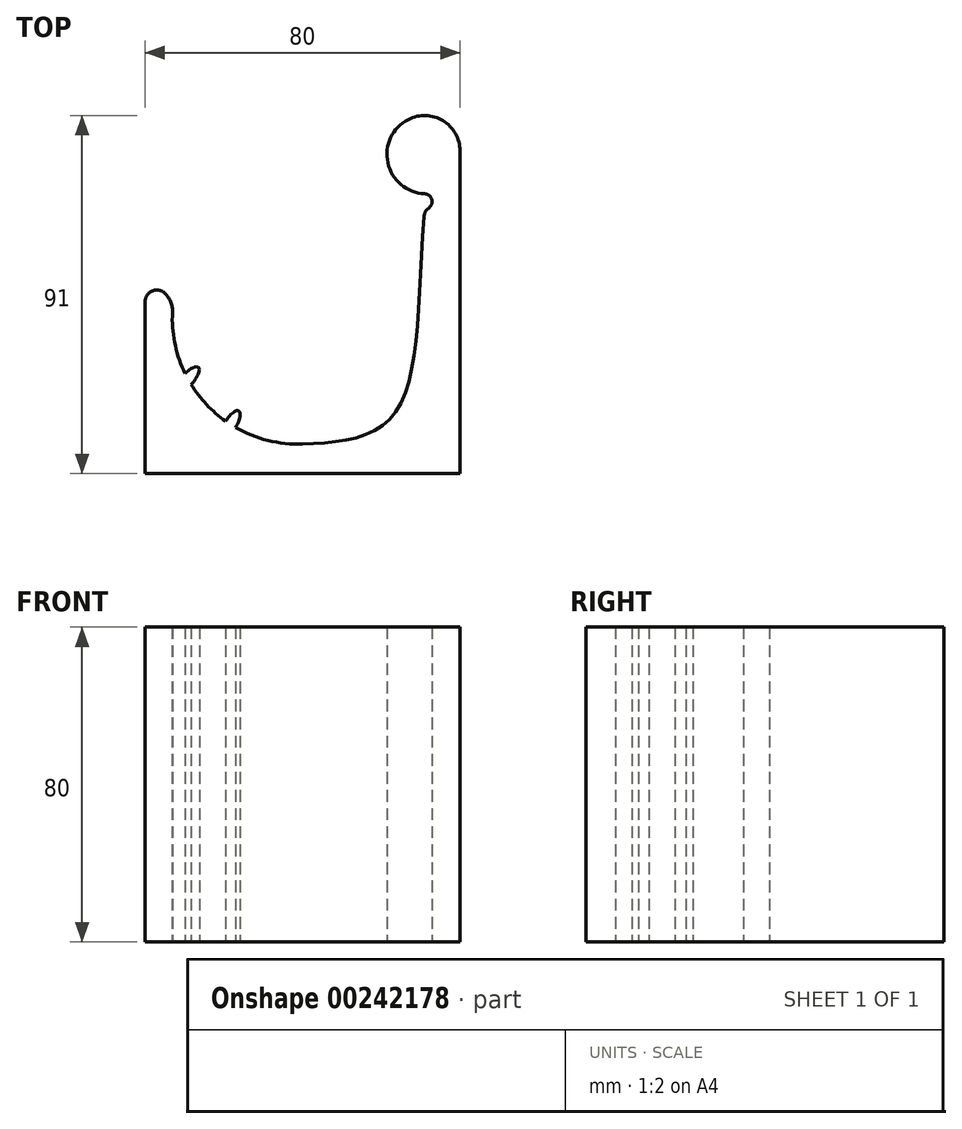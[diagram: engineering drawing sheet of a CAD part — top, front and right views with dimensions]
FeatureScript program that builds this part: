
annotation { "Feature Type Name" : "Feature", "Feature Type Description" : "" }
export const myFeature = defineFeature(function(context is Context, id is Id, definition is map)
    precondition{}
    {
        {
            var Q0;
            Q0=qCreatedBy(makeId("Top.planeOp"),FACE);
            var sketch = newSketch(context, id + "F0", { "sketchPlane" : qUnion([Q0])});
            skLineSegment(sketch, "E0.top", {"start": v(-40, -41) * mm, "end": v(40, -41) * mm});
            skLineSegment(sketch, "E0.left", {"start": v(-40, 7) * mm, "end": v(-40, -41) * mm});
            skLineSegment(sketch, "E0.right", {"start": v(40, 41) * mm, "end": v(40, -41) * mm});
            skPoint(sketch, "E0.middle", {"position": v(0, 0) * mm});
            skArc(sketch, "E1", {"start": v(40, 41) * mm, "mid": v(35.68, 48.68) * mm, "end": v(26.88, 49) * mm});
            skArc(sketch, "E2", {"start": v(26.88, 49) * mm, "mid": v(21.69, 37.98) * mm, "end": v(31, 30.12) * mm});
            skArc(sketch, "E3", {"start": v(31, 30.12) * mm, "mid": v(32.9, 28.12) * mm, "end": v(31, 26.13) * mm});
            skFitSpline(sketch, "E4", {"points": [v(31, 26.13) * mm, v(22.67, -26.58) * mm, v(0, -33.48) * mm], "startDerivative": vector(-9.3, -119.56) * mm, "endDerivative": vector(-66.14, -2.22) * mm});
            skArc(sketch, "E5", {"start": v(0, -33.48) * mm, "mid": v(-8.78, -32.56) * mm, "end": v(-16.97, -29.28) * mm});
            skPoint(sketch, "E6.orphan", {"position": v(-40, 41) * mm});
            skPoint(sketch, "E7.center.orphan", {"position": v(-42.03, 0) * mm});
            skPoint(sketch, "E8", {"position": v(-40, 0) * mm});
            skArc(sketch, "E9", {"start": v(-33.07, -1) * mm, "mid": v(-34.7, 4.58) * mm, "end": v(-40, 7) * mm});
            skPoint(sketch, "E10.orphan", {"position": v(-33.04, 0) * mm});
            skPoint(sketch, "E11", {"position": v(-29.07, -17) * mm});
            skPoint(sketch, "E11.positionSnap0", {"position": v(-40, -17) * mm});
            skPoint(sketch, "E12", {"position": v(-18.25, -28.5) * mm});
            skEllipticalArc(sketch, "E13", {});
            skEllipticalArc(sketch, "E14", {});
            skArc(sketch, "E15.trimOffspring", {"start": v(-29.8, -15.59) * mm, "mid": v(-32.3, -8.49) * mm, "end": v(-33.07, -1) * mm});
            skArc(sketch, "E16.trimOffspring", {"start": v(-19.5, -27.66) * mm, "mid": v(-24.36, -23.45) * mm, "end": v(-28.28, -18.35) * mm});
            const initialGuessF0  = {"E13": [-0.029071238616511008, -0.017, -0.6571167230125644, -0.7537888380290788, 0.004, 0.0015, 1.445669713600978, 4.5666569849899075], "E14": [-0.018251267295489836, -0.0285, 0.5215482903173446, 0.8532217653500496, 0.004, 0.0015, 4.71446657785841, 1.555279988203386]};
            skSetInitialGuess(sketch, initialGuessF0);
            skSolve(sketch);
        }
        {
            var Q0;
            Q0=makeQuery(id+"F0.imprint","IMPRINT",FACE,{"disambiguationData":[TD([[makeQuery(id+"F0.imprint","IMPRINT",EDGE,{"derivedFrom":sQuery(id+"F0.wireOp",EDGE,"E0.top")}),1.0]])]});
            extrude(context, id + "F1", {"entities" : qUnion([Q0]), "depth" : 80 * mm});
        }
        {
            var Q0;
            Q0=makeQuery(id+"F1.opExtrude","SWEPT_EDGE",EDGE,{"disambiguationData":[OSD([sQuery(id+"F0.wireOp",EDGE,"E0.left"),sQuery(id+"F0.wireOp",EDGE,"E9")])]});
            fillet(context, id + "F2", {"entities" : qUnion([Q0]), "radius" : 3 * mm, "tangentPropagation" : true, "allowEdgeOverflow" : false});
        }
        {
            var Q0;
            Q0=makeQuery(id+"F1.opExtrude","SWEPT_EDGE",EDGE,{"disambiguationData":[OSD([sQuery(id+"F0.wireOp",EDGE,"E3"),sQuery(id+"F0.wireOp",EDGE,"E4")])]});
            fillet(context, id + "F3", {"entities" : qUnion([Q0]), "radius" : 3 * mm, "tangentPropagation" : true, "allowEdgeOverflow" : false});
        }
    });
